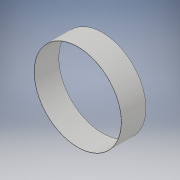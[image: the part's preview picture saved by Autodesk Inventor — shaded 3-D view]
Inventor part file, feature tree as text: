
AUTODESK INVENTOR PART (.ipt)
format: ipt  version: 2019 (Build 230136000, 136)  size: 104,448 bytes
history: native  units: mm
features: extrude x2, sketch x2
ambient origin geometry x8: Origin, YZ Plane, XZ Plane, XY Plane, X Axis, Y Axis, Z Axis, Center Point
bodies: Solid1 (feature_tree)
feature tree (4):
  extrude  "Extrusion1"  Depth=11.65mm TaperAngle=0.0deg
  extrude  "Extrusion2"  Depth=11.65mm TaperAngle=0.0deg
  sketch  "Sketch1"  dims[d0=41.668mm d1=11.65mm d2=0.0mm]
  sketch  "Sketch2"  dims[d3=41.4mm d4=11.65mm d5=0.0mm]
